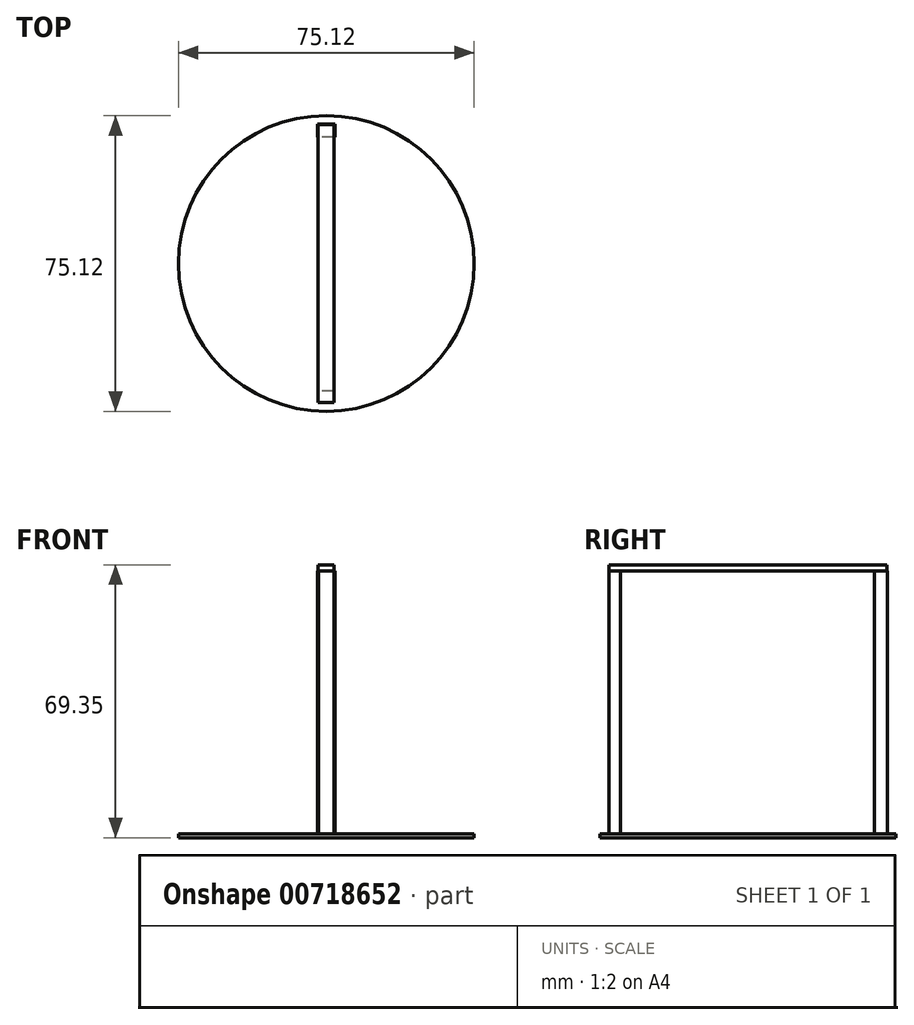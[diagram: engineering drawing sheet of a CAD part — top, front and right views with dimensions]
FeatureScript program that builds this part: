
annotation { "Feature Type Name" : "Feature", "Feature Type Description" : "" }
export const myFeature = defineFeature(function(context is Context, id is Id, definition is map)
    precondition{}
    {
        {
            var Q0;
            Q0=qCreatedBy(makeId("Top.planeOp"),FACE);
            var sketch = newSketch(context, id + "F0", { "sketchPlane" : qUnion([Q0])});
            skCircle(sketch, "E0", {"center": v(0, 0) * mm, "radius": 37.56 * mm});
            skSolve(sketch);
        }
        {
            var Q0;
            Q0=makeQuery(id+"F0.imprint","IMPRINT",FACE,{"disambiguationData":[TD([[makeQuery(id+"F0.imprint","IMPRINT",EDGE,{"derivedFrom":sQuery(id+"F0.wireOp",EDGE,"E0")}),1.0]])]});
            var sketch = newSketch(context, id + "F1", { "sketchPlane" : qUnion([Q0])});
            skLineSegment(sketch, "E1.bottom", {"start": v(1.95, -32.37) * mm, "end": v(-1.95, -32.37) * mm});
            skLineSegment(sketch, "E1.top", {"start": v(1.95, -35.35) * mm, "end": v(-1.95, -35.35) * mm});
            skLineSegment(sketch, "E1.left", {"start": v(1.95, -32.37) * mm, "end": v(1.95, -35.35) * mm});
            skLineSegment(sketch, "E1.right", {"start": v(-1.95, -32.37) * mm, "end": v(-1.95, -35.35) * mm});
            skPoint(sketch, "E1.middle", {"position": v(0, -33.86) * mm});
            skLineSegment(sketch, "E2.bottom", {"start": v(2.21, 32.17) * mm, "end": v(-2.21, 32.17) * mm});
            skLineSegment(sketch, "E2.top", {"start": v(2.21, 35.41) * mm, "end": v(-2.21, 35.41) * mm});
            skLineSegment(sketch, "E2.left", {"start": v(2.21, 32.17) * mm, "end": v(2.21, 35.41) * mm});
            skLineSegment(sketch, "E2.right", {"start": v(-2.21, 32.17) * mm, "end": v(-2.21, 35.41) * mm});
            skPoint(sketch, "E2.middle", {"position": v(0, 33.8) * mm});
            skSolve(sketch);
        }
        {
            var Q0;
            Q0 = qSketchRegion(id + "F1", true);
            extrude(context, id + "F2", {"entities" : qUnion([Q0]), "depth" : 66.8 * mm, "offsetDistance" : 25.4 * mm});
        }
        {
            var Q0;
            Q0=makeQuery(id+"F2.opExtrude","CAP_FACE",FACE,{"disambiguationData":[OSD([sQuery(id+"F1.wireOp",EDGE,"E1.bottom"),sQuery(id+"F1.wireOp",EDGE,"E1.top"),sQuery(id+"F1.wireOp",EDGE,"E1.left"),sQuery(id+"F1.wireOp",EDGE,"E1.right")])],"isStart":false});
            var sketch = newSketch(context, id + "F3", { "sketchPlane" : qUnion([Q0])});
            skLineSegment(sketch, "E3.bottom", {"start": v(1.95, -35.35) * mm, "end": v(-2.15, -35.35) * mm});
            skLineSegment(sketch, "E3.top", {"start": v(1.95, 35.36) * mm, "end": v(-2.15, 35.36) * mm});
            skLineSegment(sketch, "E3.left", {"start": v(1.95, -35.35) * mm, "end": v(1.95, 35.36) * mm});
            skLineSegment(sketch, "E3.right", {"start": v(-2.15, -35.35) * mm, "end": v(-2.15, 35.36) * mm});
            skSolve(sketch);
        }
        {
            var Q0;
            Q0 = qSketchRegion(id + "F3", true);
            extrude(context, id + "F4", {"entities" : qUnion([Q0]), "depth" : 1.52 * mm, "offsetDistance" : 25.4 * mm});
        }
        {
            var Q0;
            Q0=makeQuery(id+"F0.imprint","IMPRINT",FACE,{"disambiguationData":[TD([[makeQuery(id+"F0.imprint","IMPRINT",EDGE,{"derivedFrom":sQuery(id+"F0.wireOp",EDGE,"E0")}),1.0]])]});
            extrude(context, id + "F5", {"entities" : qUnion([Q0]), "oppositeDirection" : true, "depth" : 1.02 * mm, "offsetDistance" : 25.4 * mm});
        }
        {
            var Q0;
            Q0=makeQuery(id+"F5.opExtrude","CAP_FACE",FACE,{"disambiguationData":[OSD([sQuery(id+"F0.wireOp",EDGE,"E0")])],"isStart":true});
            var sketch = newSketch(context, id + "F6", { "sketchPlane" : qUnion([Q0])});
            skArc(sketch, "E4", {"start": v(0, 0) * mm, "mid": v(-12.2, 8.52) * mm, "end": v(-24.4, 0) * mm});
            skArc(sketch, "E5", {"start": v(0, 0) * mm, "mid": v(7.39, 11.73) * mm, "end": v(0, 23.45) * mm});
            skSolve(sketch);
        }
        {
            var Q0;
            Q0=sQuery(id+"F6.wireOp",EDGE,"E4");
            var Q1;
            Q1=sQuery(id+"F6.wireOp",EDGE,"E5");
            extrude(context, id + "F7", {"bodyType" : ToolBodyType.SURFACE, "surfaceEntities" : qUnion([Q0, Q1]), "depth" : 63.5 * mm, "offsetDistance" : 25 * mm});
        }
        {
            var Q0;
            Q0=makeQuery(id+"F5.opExtrude","CAP_FACE",FACE,{"disambiguationData":[OSD([sQuery(id+"F0.wireOp",EDGE,"E0")])],"isStart":true});
            var sketch = newSketch(context, id + "F8", { "sketchPlane" : qUnion([Q0])});
            skArc(sketch, "E6", {"start": v(0, 0) * mm, "mid": v(12.48, -9.37) * mm, "end": v(24.96, 0) * mm});
            skArc(sketch, "E7", {"start": v(0, 0) * mm, "mid": v(-11.14, -12.87) * mm, "end": v(0, -25.73) * mm});
            skSolve(sketch);
        }
        {
            var Q0;
            Q0=sQuery(id+"F8.wireOp",EDGE,"E7");
            var Q1;
            Q1=sQuery(id+"F8.wireOp",EDGE,"E6");
            extrude(context, id + "F9", {"bodyType" : ToolBodyType.SURFACE, "surfaceEntities" : qUnion([Q0, Q1]), "depth" : 63.5 * mm, "offsetDistance" : 25 * mm});
        }
    });
